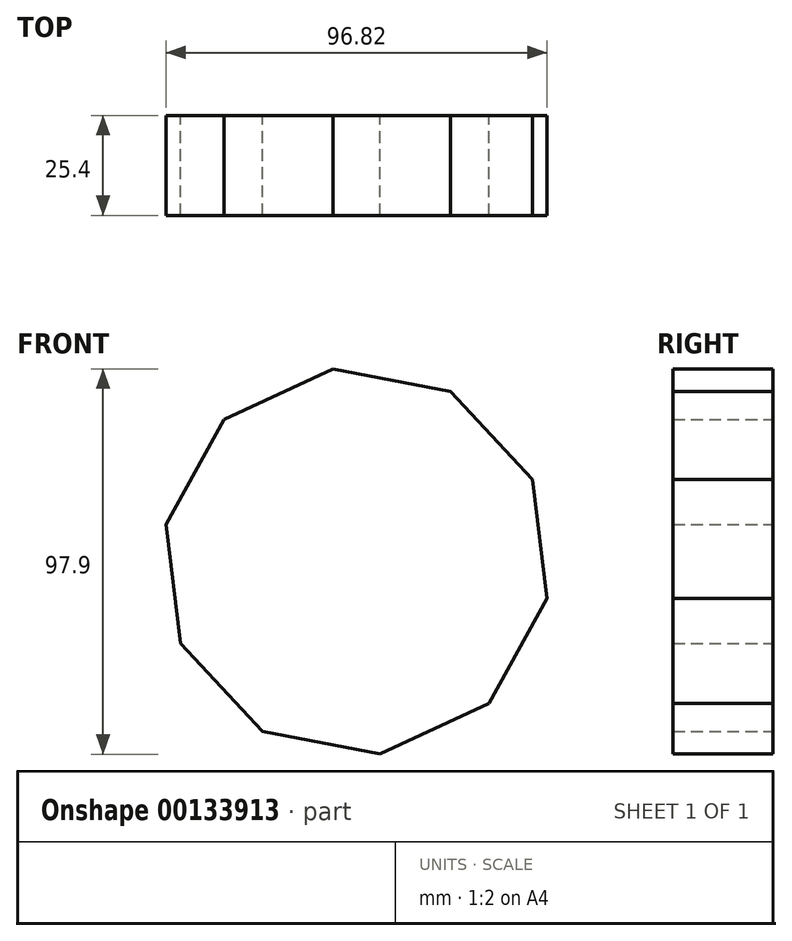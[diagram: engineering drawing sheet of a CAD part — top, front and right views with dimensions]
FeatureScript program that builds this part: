
annotation { "Feature Type Name" : "Feature", "Feature Type Description" : "" }
export const myFeature = defineFeature(function(context is Context, id is Id, definition is map)
    precondition{}
    {
        {
            var Q0;
            Q0=qCreatedBy(makeId("Front.planeOp"),FACE);
            var sketch = newSketch(context, id + "F0", { "sketchPlane" : qUnion([Q0])});
            skCircle(sketch, "E0.cCircle", {"center": v(0, -25.15) * mm, "radius": 46.9 * mm, "construction": true});
            skLineSegment(sketch, "E0.0", {"start": v(33.65, -61.2) * mm, "end": v(6.02, -74.1) * mm});
            skLineSegment(sketch, "E0.1", {"start": v(6.02, -74.1) * mm, "end": v(-23.9, -68.29) * mm});
            skLineSegment(sketch, "E0.2", {"start": v(-23.9, -68.29) * mm, "end": v(-44.7, -46) * mm});
            skLineSegment(sketch, "E0.3", {"start": v(-44.7, -46) * mm, "end": v(-48.41, -15.75) * mm});
            skLineSegment(sketch, "E0.4", {"start": v(-48.41, -15.75) * mm, "end": v(-33.65, 10.91) * mm});
            skLineSegment(sketch, "E0.5", {"start": v(-33.65, 10.91) * mm, "end": v(-6.02, 23.8) * mm});
            skLineSegment(sketch, "E0.6", {"start": v(-6.02, 23.8) * mm, "end": v(23.9, 18) * mm});
            skLineSegment(sketch, "E0.7", {"start": v(23.9, 18) * mm, "end": v(44.7, -4.3) * mm});
            skLineSegment(sketch, "E0.8", {"start": v(44.7, -4.3) * mm, "end": v(48.41, -34.54) * mm});
            skLineSegment(sketch, "E0.9", {"start": v(48.41, -34.54) * mm, "end": v(33.65, -61.2) * mm});
            skPoint(sketch, "E0.0.midPoint", {"position": v(19.83, -67.65) * mm});
            skSolve(sketch);
        }
        {
            var Q0;
            Q0 = qSketchRegion(id + "F0", true);
            extrude(context, id + "F1", {"entities" : qUnion([Q0]), "depth" : 25.4 * mm});
        }
    });
